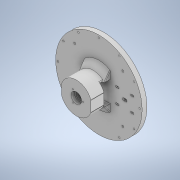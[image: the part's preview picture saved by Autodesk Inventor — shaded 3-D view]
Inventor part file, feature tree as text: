
AUTODESK INVENTOR PART (.ipt)
format: ipt  version: 2020.3 (Build 243373000, 373)  size: 467,968 bytes
history: native  units: mm
features: extrude x19, sketch x19, pattern_circular x3, pattern_linear x1, chamfer x1, fillet x1
ambient origin geometry x8: Origin, YZ Plane, XZ Plane, XY Plane, X Axis, Y Axis, Z Axis, Center Point
bodies: Solid1 (feature_tree)
feature tree (44):
  extrude  "Extrusion1"  Depth=22.0mm
  extrude  "Extrusion2"  Depth=8.6mm
  extrude  "Extrusion3"  Depth=2.0mm
  extrude  "Extrusion4"  Depth=10.0mm TaperAngle=0.0deg
  extrude  "Extrusion5"  Depth=10.0mm
  extrude  "Extrusion6"  Depth=22.0mm
  extrude  "Extrusion7"  Depth=47.0mm TaperAngle=0.0deg
  extrude  "Extrusion11"  Depth=14.0mm
  pattern_circular  "Circular Pattern1"  Count=3 Angle=360.0deg
  extrude  "Extrusion14"  Depth=7.2mm TaperAngle=0.0deg
  extrude  "Extrusion18"  Depth=3.2mm
  extrude  "Extrusion19"  Depth=10.0mm TaperAngle=0.0deg
  pattern_circular  "Circular Pattern3"  Count=11 Angle=300.0deg
  extrude  "Extrusion20"  Depth=2.7mm
  extrude  "Extrusion21"  Depth=54.0mm
  extrude  "Extrusion22"  Depth=4.0mm
  extrude  "Extrusion23"  Depth=15.5mm
  pattern_circular  "Circular Pattern4"  [2 undecoded]
  extrude  "Extrusion24"  Depth=2.0mm TaperAngle=0.0deg
  pattern_linear  "Rectangular Pattern2"  Spacing1=120.0deg  [1 undecoded]
  chamfer  "Chamfer2"  Angle=120.0deg  [1 undecoded]
  extrude  "Extrusion25"  Depth=2.0mm
  extrude  "Extrusion27"  Depth=2.0mm
  fillet  "Fillet4"  Radius=50.0mm
  extrude  "Extrusion28"  Depth=2.0mm
  sketch  "Sketch1"  dims[d0=180.0mm d1=22.0mm]
  sketch  "Sketch3"  dims[d2=8.0mm d3=0.0mm d4=8.6mm]
  sketch  "Sketch4"  dims[d5=2.0mm d6=0.0mm d7=45.0mm]
  sketch  "Sketch5"  dims[d8=10.0mm d9=20.0mm d10=0.0mm]
  sketch  "Sketch6"  dims[d13=10.0mm d14=0.0mm d15=8.6mm]
  sketch  "Sketch7"  dims[d16=20.0mm d17=0.0mm d18=22.0mm]
  sketch  "Sketch8"  dims[d19=7.0mm d20=0.0mm d23=47.0mm d24=0.0mm]
  sketch  "Sketch12"  dims[d43=2.5mm d44=14.0mm]
  sketch  "Sketch17"  dims[d45=15.0mm d46=0.0mm d47=30.0mm d48=360.0deg]
  sketch  "Sketch21"  dims[d62=15.0mm d63=7.2mm d64=0.0mm]
  sketch  "Sketch22"  dims[d87=85.0mm d88=3.2mm]
  sketch  "Sketch23"  dims[d89=10.0mm d90=0.0mm d92=5.0mm d93=0.0mm d94=110.0mm d95=300.0deg]
  sketch  "Sketch24"  dims[d97=210.0deg d98=2.7mm]
  sketch  "Sketch26"  dims[d99=4.0mm d100=54.0mm]
  sketch  "Sketch27"  dims[d105=1.6mm d107=4.0mm]
  sketch  "Sketch28"  dims[d108=15.5mm d109=15.5mm]
  sketch  "Sketch29"  dims[d110=10.0mm d111=0.0mm]
  sketch  "Sketch31"  dims[d112=21.5mm]
  sketch  "Sketch32"  dims[d113=10.0mm d114=0.0mm d115=3.5mm d116=4.0mm d117=0.0mm d124=120.0deg d125=120.0deg d126=5.7mm d127=4.0mm d128=50.0mm d129=50.0mm d130=10.0mm d131=0.0mm d132=40.0mm d133=360.0deg d135=10.0mm d136=0.0mm d137=20.0mm d139=31.0mm d140=20.0mm d142=31.0mm d143=0.174533mm d144=0.349066mm d145=12.0mm d146=2.0mm d147=45.0deg d148=20.0mm d149=40.0mm d150=40.0mm d151=15.0mm d152=0.0mm d161=40.0mm d162=40.0mm d163=20.0mm d164=30.0mm d165=0.0mm d166=2.0mm d167=0.5mm d168=0.0mm]
note: 4 required parameter values undecoded (feature->parameter linkage not recoverable at this tier; creation-order binding heuristic only, values carry confidence <= 0.55)
